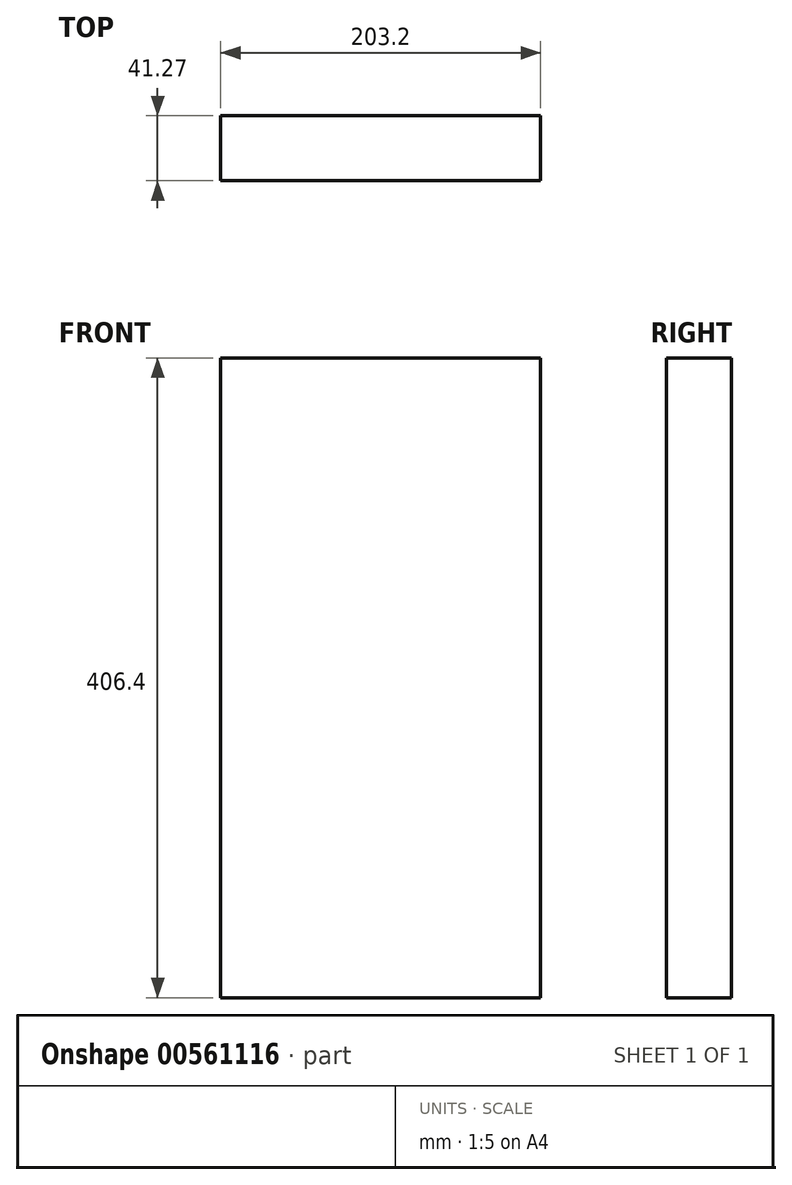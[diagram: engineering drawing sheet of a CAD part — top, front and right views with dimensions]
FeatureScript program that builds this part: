
annotation { "Feature Type Name" : "Feature", "Feature Type Description" : "" }
export const myFeature = defineFeature(function(context is Context, id is Id, definition is map)
    precondition{}
    {
        {
            var Q0;
            Q0=qCreatedBy(makeId("Front.planeOp"),FACE);
            var sketch = newSketch(context, id + "F0", { "sketchPlane" : qUnion([Q0])});
            skLineSegment(sketch, "E0.bottom", {"start": v(0, 0) * mm, "end": v(203.2, 0) * mm});
            skLineSegment(sketch, "E0.top", {"start": v(0, 406.4) * mm, "end": v(203.2, 406.4) * mm});
            skLineSegment(sketch, "E0.left", {"start": v(0, 0) * mm, "end": v(0, 406.4) * mm});
            skLineSegment(sketch, "E0.right", {"start": v(203.2, 0) * mm, "end": v(203.2, 406.4) * mm});
            skSolve(sketch);
        }
        {
            var Q0;
            Q0=makeQuery(id+"F0.imprint","IMPRINT",FACE,{"disambiguationData":[TD([[makeQuery(id+"F0.imprint","IMPRINT",EDGE,{"derivedFrom":sQuery(id+"F0.wireOp",EDGE,"E0.bottom")}),1.0]])]});
            extrude(context, id + "F1", {"entities" : qUnion([Q0]), "depth" : 41.27 * mm, "offsetDistance" : 25.4 * mm});
        }
    });
